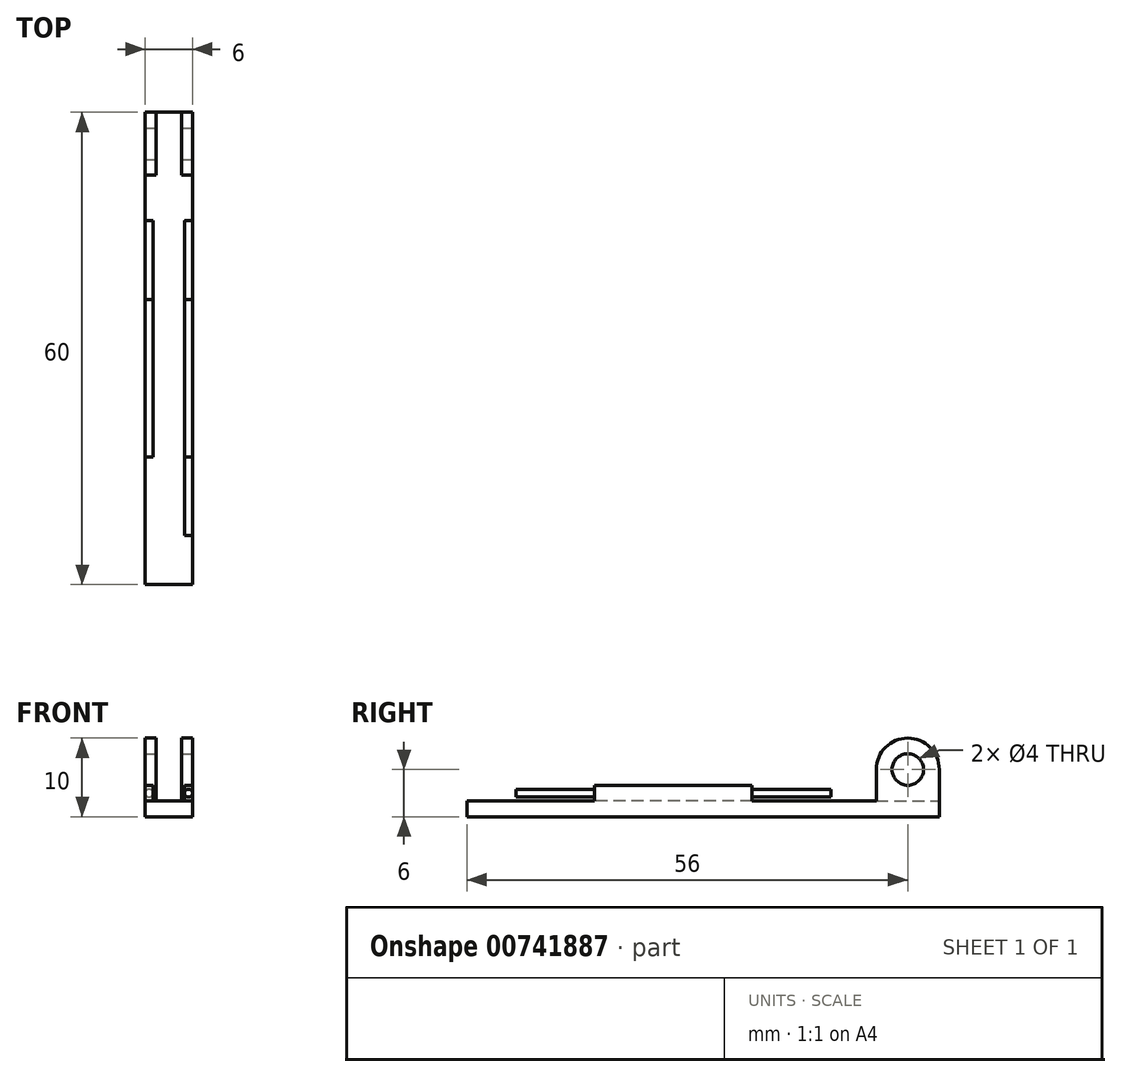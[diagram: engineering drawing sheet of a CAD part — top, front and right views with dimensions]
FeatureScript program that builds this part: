
annotation { "Feature Type Name" : "Feature", "Feature Type Description" : "" }
export const myFeature = defineFeature(function(context is Context, id is Id, definition is map)
    precondition{}
    {
        {
            var Q0;
            Q0=qCreatedBy(makeId("Top.planeOp"),FACE);
            var sketch = newSketch(context, id + "F0", { "sketchPlane" : qUnion([Q0])});
            skLineSegment(sketch, "E0.bottom", {"start": v(-3, 30) * mm, "end": v(3, 30) * mm});
            skLineSegment(sketch, "E0.top", {"start": v(-3, -30) * mm, "end": v(3, -30) * mm});
            skLineSegment(sketch, "E0.left", {"start": v(-3, 30) * mm, "end": v(-3, -30) * mm});
            skLineSegment(sketch, "E0.right", {"start": v(3, 30) * mm, "end": v(3, -30) * mm});
            skSolve(sketch);
        }
        {
            var Q0;
            Q0 = qSketchRegion(id + "F0", true);
            extrude(context, id + "F1", {"entities" : qUnion([Q0]), "depth" : 2 * mm, "offsetDistance" : 25 * mm});
        }
        {
            var Q0;
            Q0=makeQuery(id+"F1.opExtrude","SWEPT_FACE",FACE,{"disambiguationData":[OSD([sQuery(id+"F0.wireOp",EDGE,"E0.right")])]});
            var sketch = newSketch(context, id + "F2", { "sketchPlane" : qUnion([Q0])});
            skLineSegment(sketch, "E1", {"start": v(30, 2) * mm, "end": v(30, 6) * mm});
            skLineSegment(sketch, "E2", {"start": v(30, 6) * mm, "end": v(30, 6) * mm});
            skCircle(sketch, "E3", {"center": v(26, 6) * mm, "radius": 2 * mm});
            skPoint(sketch, "E4.trimOffspring.end.orphan", {"position": v(22, 6) * mm});
            skLineSegment(sketch, "E5", {"start": v(30, 6) * mm, "end": v(22, 6) * mm});
            skLineSegment(sketch, "E6", {"start": v(22, 6) * mm, "end": v(22, 2) * mm});
            skArc(sketch, "E7", {"start": v(30, 6) * mm, "mid": v(26, 10) * mm, "end": v(22, 6) * mm});
            skSolve(sketch);
        }
        {
            var Q0;
            {var subQ4=sQuery(id+"F2.wireOp",EDGE,"E7");Q0=makeQuery(id+"F2.imprint","IMPRINT",FACE,{"disambiguationData":[TD([[makeQuery(id+"F2.imprint","IMPRINT",EDGE,{"derivedFrom":subQ4}),1.0]])]});}
            var Q1;
            {var subQ2=sQuery(id+"F2.wireOp",EDGE,"E1");Q1=makeQuery(id+"F2.imprint","IMPRINT",FACE,{"disambiguationData":[TD([[makeQuery(id+"F2.imprint","IMPRINT",EDGE,{"derivedFrom":subQ2}),1.0]])]});}
            extrude(context, id + "F3", {"entities" : qUnion([Q0, Q1]), "operationType" : NewBodyOperationType.ADD, "oppositeDirection" : true, "depth" : 6 * mm, "offsetDistance" : 25 * mm});
        }
        {
            var Q0;
            Q0=makeQuery(id+"F1.opExtrude","CAP_FACE",FACE,{"disambiguationData":[OSD([sQuery(id+"F0.wireOp",EDGE,"E0.bottom"),sQuery(id+"F0.wireOp",EDGE,"E0.top"),sQuery(id+"F0.wireOp",EDGE,"E0.left"),sQuery(id+"F0.wireOp",EDGE,"E0.right")])],"isStart":false});
            var sketch = newSketch(context, id + "F4", { "sketchPlane" : qUnion([Q0])});
            skLineSegment(sketch, "E8.bottom", {"start": v(3, 6.23) * mm, "end": v(2, 6.23) * mm});
            skLineSegment(sketch, "E8.top", {"start": v(3, -13.77) * mm, "end": v(2, -13.77) * mm});
            skLineSegment(sketch, "E8.left", {"start": v(3, 6.23) * mm, "end": v(3, -13.77) * mm});
            skLineSegment(sketch, "E8.right", {"start": v(2, 6.23) * mm, "end": v(2, -13.77) * mm});
            skLineSegment(sketch, "E9", {"start": v(3, 22) * mm, "end": v(3, 12) * mm});
            skLineSegment(sketch, "E10.MirrorCS", {"start": v(-2, 6.23) * mm, "end": v(-2, -13.77) * mm});
            skLineSegment(sketch, "E11.MirrorCS", {"start": v(-3, 6.23) * mm, "end": v(-3, -13.77) * mm});
            skLineSegment(sketch, "E12.MirrorCS", {"start": v(-3, 6.23) * mm, "end": v(-2, 6.23) * mm});
            skLineSegment(sketch, "E13.MirrorCS", {"start": v(-3, -13.77) * mm, "end": v(-2, -13.77) * mm});
            skSolve(sketch);
        }
        {
            var Q0;
            {var subQ2=sQuery(id+"F4.wireOp",EDGE,"E8.bottom");Q0=makeQuery(id+"F4.imprint","IMPRINT",FACE,{"disambiguationData":[TD([[makeQuery(id+"F4.imprint","IMPRINT",EDGE,{"derivedFrom":subQ2}),-1.0]])]});}
            var sketch = newSketch(context, id + "F5", { "sketchPlane" : qUnion([Q0])});
            skLineSegment(sketch, "E14.0.1", {"start": v(1.6, 30) * mm, "end": v(-1.6, 30) * mm});
            skLineSegment(sketch, "E14.0.3", {"start": v(-1.6, 22) * mm, "end": v(1.6, 22) * mm});
            skLineSegment(sketch, "E15", {"start": v(0, 30) * mm, "end": v(0, 22) * mm, "construction": true});
            skLineSegment(sketch, "E16", {"start": v(0, 30) * mm, "end": v(1.6, 30) * mm});
            skLineSegment(sketch, "E17", {"start": v(-1.6, 30) * mm, "end": v(-1.6, 22) * mm});
            skLineSegment(sketch, "E18", {"start": v(1.6, 22) * mm, "end": v(1.6, 30) * mm});
            skSolve(sketch);
        }
        {
            var Q0;
            Q0 = qSketchRegion(id + "F5", true);
            extrude(context, id + "F6", {"entities" : qUnion([Q0]), "operationType" : NewBodyOperationType.REMOVE, "depth" : 25 * mm, "offsetDistance" : 25 * mm});
        }
        {
            var Q0;
            Q0 = qSketchRegion(id + "F4", true);
            extrude(context, id + "F7", {"entities" : qUnion([Q0]), "operationType" : NewBodyOperationType.ADD, "depth" : 2 * mm, "offsetDistance" : 25 * mm});
        }
        {
            var Q0;
            Q0=makeQuery(id+"F7.opExtrude","SWEPT_FACE",FACE,{"disambiguationData":[OSD([sQuery(id+"F4.wireOp",EDGE,"E8.top")])]});
            var sketch = newSketch(context, id + "F8", { "sketchPlane" : qUnion([Q0])});
            skLineSegment(sketch, "E19", {"start": v(2, 4) * mm, "end": v(3, 4) * mm});
            skLineSegment(sketch, "E20", {"start": v(2.5, 4) * mm, "end": v(2.5, 3) * mm});
            skCircle(sketch, "E21", {"center": v(2.5, 3) * mm, "radius": 0.5 * mm});
            skCircle(sketch, "E22.MirrorC", {"center": v(-2.5, 3) * mm, "radius": 0.5 * mm});
            skLineSegment(sketch, "E23.MirrorCS", {"start": v(-2.5, 4) * mm, "end": v(-2.5, 3) * mm});
            skSolve(sketch);
        }
        {
            var Q0;
            {var subQ0=sQuery(id+"F8.wireOp",EDGE,"E21");var subQ1=makeQuery(id+"F8.imprint","INTERSECT",VERTEX,{"derivedFrom":[sQuery(id+"F8.wireOp",EDGE,"E20"),subQ0]});Q0=makeQuery(id+"F8.imprint","IMPRINT",FACE,{"disambiguationData":[TD([[makeQuery(id+"F8.imprint","IMPRINT",EDGE,{"disambiguationData":[TD([[subQ1,-1.0]])],"derivedFrom":subQ0}),1.0]])]});}
            var Q1;
            Q1=makeQuery(id+"F8.imprint","IMPRINT",FACE,{"disambiguationData":[TD([[makeQuery(id+"F8.imprint","IMPRINT",EDGE,{"derivedFrom":sQuery(id+"F8.wireOp",EDGE,"E22.MirrorC")}),-1.0]])]});
            extrude(context, id + "F9", {"entities" : qUnion([Q0, Q1]), "operationType" : NewBodyOperationType.ADD, "depth" : 10 * mm, "offsetDistance" : 25 * mm});
        }
        {
            var Q0;
            Q0=makeQuery(id+"F7.opExtrude","SWEPT_FACE",FACE,{"disambiguationData":[OSD([sQuery(id+"F4.wireOp",EDGE,"E8.bottom")])]});
            var sketch = newSketch(context, id + "F10", { "sketchPlane" : qUnion([Q0])});
            skCircle(sketch, "E24.0", {"center": v(-2.5, 3) * mm, "radius": 0.5 * mm});
            skCircle(sketch, "E25.0", {"center": v(2.5, 3) * mm, "radius": 0.5 * mm});
            skSolve(sketch);
        }
        {
            var Q0;
            Q0 = qSketchRegion(id + "F10", true);
            extrude(context, id + "F11", {"entities" : qUnion([Q0]), "operationType" : NewBodyOperationType.ADD, "depth" : 10 * mm, "offsetDistance" : 25 * mm});
        }
        {
            var Q0;
            Q0=makeQuery(id+"F9.opExtrude","CAP_FACE",FACE,{"disambiguationData":[OSD([sQuery(id+"F8.wireOp",EDGE,"E21")])],"isStart":false});
            var sketch = newSketch(context, id + "F12", { "sketchPlane" : qUnion([Q0])});
            skPoint(sketch, "E26.0", {"position": v(2.5, 3) * mm});
            skCircle(sketch, "E27.0.0", {"center": v(2.5, 3) * mm, "radius": 0.5 * mm});
            skArc(sketch, "E28.0", {"start": v(2.99, 3.35) * mm, "mid": v(1.93, 2.82) * mm, "end": v(3.1, 3) * mm});
            skFitSpline(sketch, "E29", {"points": [v(3.1, 3) * mm, v(3.4, 6.14) * mm, v(3.19, 10.8) * mm, v(0, 11.63) * mm], "startDerivative": vector(0.67, 8.98) * mm, "endDerivative": vector(-12.37, 0.04) * mm});
            skSolve(sketch);
        }
        {
            var Q0;
            Q0 = qSketchRegion(id + "F12", true);
            var Q1;
            Q1=sQuery(id+"F12.wireOp",EDGE,"E29");
            extrude(context, id + "F13", {"entities" : qUnion([Q0]), "bodyType" : ToolBodyType.SURFACE, "surfaceEntities" : qUnion([Q1]), "oppositeDirection" : true, "depth" : 55.1 * mm, "offsetDistance" : 25 * mm, "hasSecondDirection" : true, "secondDirectionOppositeDirection" : false, "secondDirectionDepth" : 6.18 * mm});
        }
        {
            var Q0;
            Q0=qCreatedBy(makeId("Top.planeOp"),FACE);
            var sketch = newSketch(context, id + "F14", { "sketchPlane" : qUnion([Q0])});
            skLineSegment(sketch, "E30", {"start": v(-3, 6.23) * mm, "end": v(-3, 16.23) * mm});
            skLineSegment(sketch, "E31", {"start": v(-2, 16.23) * mm, "end": v(-2, 6.23) * mm});
            skFitSpline(sketch, "E32", {"points": [v(-2, 6.51) * mm, v(-3, 6.5) * mm, v(-3.35, -14.8) * mm], "startDerivative": vector(-6.06, 2.19) * mm, "endDerivative": vector(1.73, -36.3) * mm});
            skLineSegment(sketch, "E33", {"start": v(-2, -13.77) * mm, "end": v(-2, -23.77) * mm});
            skLineSegment(sketch, "E34", {"start": v(-3, -23.77) * mm, "end": v(-3, -13.77) * mm});
            skFitSpline(sketch, "E35", {"points": [v(-3.35, -14.8) * mm, v(-3, -14.8) * mm, v(-2, -14.8) * mm], "startDerivative": vector(0.83, 0) * mm, "endDerivative": vector(1.8, 0) * mm});
            skFitSpline(sketch, "E36.MirrorCS", {"points": [v(2, 6.51) * mm, v(3, 6.5) * mm, v(3.35, -14.8) * mm], "startDerivative": vector(6.06, 2.19) * mm, "endDerivative": vector(-1.73, -36.3) * mm});
            skFitSpline(sketch, "E37.MirrorCS", {"points": [v(3.35, -14.8) * mm, v(3, -14.8) * mm, v(2, -14.8) * mm], "startDerivative": vector(-0.83, 0) * mm, "endDerivative": vector(-1.8, 0) * mm});
            skSolve(sketch);
        }
        {
            var Q0;
            Q0=sQuery(id+"F12.wireOp",EDGE,"E28.0");
            extrude(context, id + "F15", {"bodyType" : ToolBodyType.SURFACE, "surfaceEntities" : qUnion([Q0]), "oppositeDirection" : true, "depth" : 8 * mm, "offsetDistance" : 25 * mm, "hasSecondDirection" : true, "secondDirectionOppositeDirection" : false, "secondDirectionDepth" : 6.18 * mm});
        }
        {
            var Q0;
            Q0=makeQuery(id+"F13.opExtrude","SWEPT_BODY",BODY,{"disambiguationData":[OSD([sQuery(id+"F12.wireOp",EDGE,"E29")])]});
            var Q1;
            Q1=makeQuery(id+"F15.opExtrude","SWEPT_BODY",BODY,{"disambiguationData":[OSD([sQuery(id+"F12.wireOp",EDGE,"E28.0")])]});
            var Q2;
            Q2=qCreatedBy(makeId("Right.planeOp"),FACE);
            mirror(context, id + "F16", {"entities" : qUnion([Q0, Q1]), "mirrorPlane" : qUnion([Q2])});
        }
        {
            var Q0;
            Q0=makeQuery(id+"F7.boolean.opBoolean","MERGE",FACE,{"derivedFrom":[makeQuery(id+"F3.boolean.opBoolean","MERGE",FACE,{"derivedFrom":[makeQuery(id+"F1.opExtrude","SWEPT_FACE",FACE,{"disambiguationData":[OSD([sQuery(id+"F0.wireOp",EDGE,"E0.left")])]}),makeQuery(id+"F3.opExtrude","CAP_FACE",FACE,{"disambiguationData":[OSD([sQuery(id+"F0.wireOp",EDGE,"E0.right"),sQuery(id+"F2.wireOp",EDGE,"E1"),sQuery(id+"F2.wireOp",EDGE,"E3"),sQuery(id+"F2.wireOp",EDGE,"E6"),sQuery(id+"F2.wireOp",EDGE,"E7")])],"isStart":false})]}),makeQuery(id+"F7.opExtrude","SWEPT_FACE",FACE,{"disambiguationData":[OSD([sQuery(id+"F4.wireOp",EDGE,"E11.MirrorCS")])]})]});
            var sketch = newSketch(context, id + "F17", { "sketchPlane" : qUnion([Q0])});
            skFitSpline(sketch, "E38", {"points": [v(30, 0) * mm, v(32.78, 2.39) * mm, v(15.35, 15.38) * mm, v(-23.16, 16.68) * mm, v(-30, 6) * mm, v(-30, 0) * mm], "startDerivative": vector(40.18, 17.81) * mm, "endDerivative": vector(4.14, -41.96) * mm});
            skSolve(sketch);
        }
        {
            var Q0;
            Q0 = qSketchRegion(id + "F17", true);
            var Q1;
            Q1=sQuery(id+"F17.wireOp",EDGE,"E38");
            extrude(context, id + "F18", {"entities" : qUnion([Q0]), "bodyType" : ToolBodyType.SURFACE, "surfaceEntities" : qUnion([Q1]), "oppositeDirection" : true, "depth" : 6.1 * mm, "offsetDistance" : 25 * mm});
        }
    });
